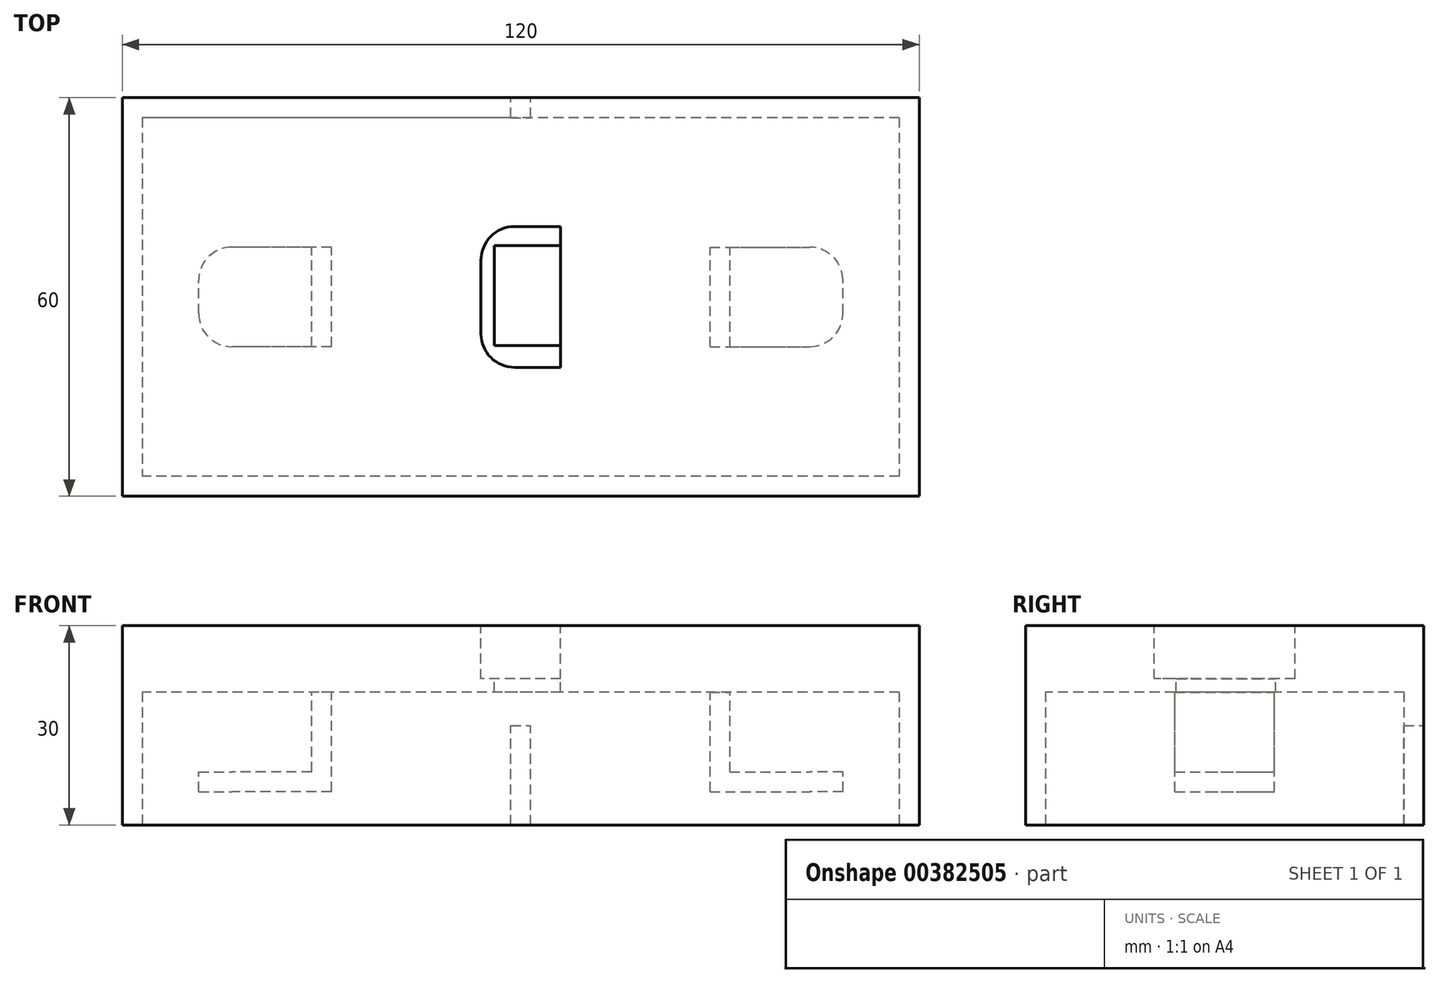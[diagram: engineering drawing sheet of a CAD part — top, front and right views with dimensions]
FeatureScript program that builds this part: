
annotation { "Feature Type Name" : "Feature", "Feature Type Description" : "" }
export const myFeature = defineFeature(function(context is Context, id is Id, definition is map)
    precondition{}
    {
        {
            var Q0;
            Q0=qCreatedBy(makeId("Top.planeOp"),FACE);
            var sketch = newSketch(context, id + "F0", { "sketchPlane" : qUnion([Q0])});
            skLineSegment(sketch, "E0.bottom", {"start": v(60, 30) * mm, "end": v(-60, 30) * mm});
            skLineSegment(sketch, "E0.top", {"start": v(60, -30) * mm, "end": v(-60, -30) * mm});
            skLineSegment(sketch, "E0.left", {"start": v(60, 30) * mm, "end": v(60, -30) * mm});
            skLineSegment(sketch, "E0.right", {"start": v(-60, 30) * mm, "end": v(-60, -30) * mm});
            skPoint(sketch, "E0.middle", {"position": v(0, 0) * mm});
            skSolve(sketch);
        }
        {
            var Q0;
            Q0 = qSketchRegion(id + "F0", true);
            extrude(context, id + "F1", {"entities" : qUnion([Q0]), "depth" : 30 * mm});
        }
        {
            var Q0;
            Q0=makeQuery(id+"F1.opExtrude","CAP_FACE",FACE,{"disambiguationData":[OSD([sQuery(id+"F0.wireOp",EDGE,"E0.bottom"),sQuery(id+"F0.wireOp",EDGE,"E0.top"),sQuery(id+"F0.wireOp",EDGE,"E0.left"),sQuery(id+"F0.wireOp",EDGE,"E0.right")])],"isStart":false});
            var sketch = newSketch(context, id + "F2", { "sketchPlane" : qUnion([Q0])});
            skLineSegment(sketch, "E1.bottom", {"start": v(6, 10.6) * mm, "end": v(-6, 10.6) * mm});
            skLineSegment(sketch, "E1.top", {"start": v(6, -10.6) * mm, "end": v(-6, -10.6) * mm});
            skLineSegment(sketch, "E1.left", {"start": v(6, 10.6) * mm, "end": v(6, -10.6) * mm});
            skLineSegment(sketch, "E1.right", {"start": v(-6, 10.6) * mm, "end": v(-6, -10.6) * mm});
            skPoint(sketch, "E1.middle", {"position": v(0, 0) * mm});
            skSolve(sketch);
        }
        {
            var Q0;
            Q0 = qSketchRegion(id + "F2", true);
            extrude(context, id + "F3", {"entities" : qUnion([Q0]), "operationType" : NewBodyOperationType.REMOVE, "oppositeDirection" : true, "depth" : 8 * mm});
        }
        {
            var Q0;
            Q0=makeQuery(id+"F1.opExtrude","CAP_FACE",FACE,{"disambiguationData":[OSD([sQuery(id+"F0.wireOp",EDGE,"E0.bottom"),sQuery(id+"F0.wireOp",EDGE,"E0.top"),sQuery(id+"F0.wireOp",EDGE,"E0.left"),sQuery(id+"F0.wireOp",EDGE,"E0.right")])],"isStart":true});
            var sketch = newSketch(context, id + "F4", { "sketchPlane" : qUnion([Q0])});
            skLineSegment(sketch, "E2.bottom", {"start": v(57, -27) * mm, "end": v(-57, -27) * mm});
            skLineSegment(sketch, "E2.top", {"start": v(57, 27) * mm, "end": v(-57, 27) * mm});
            skLineSegment(sketch, "E2.left", {"start": v(57, -27) * mm, "end": v(57, 27) * mm});
            skLineSegment(sketch, "E2.right", {"start": v(-57, -27) * mm, "end": v(-57, 27) * mm});
            skPoint(sketch, "E2.middle", {"position": v(0, 0) * mm});
            skSolve(sketch);
        }
        {
            var Q0;
            Q0 = qSketchRegion(id + "F4", true);
            extrude(context, id + "F5", {"entities" : qUnion([Q0]), "operationType" : NewBodyOperationType.REMOVE, "oppositeDirection" : true, "depth" : 20 * mm});
        }
        {
            var Q0;
            Q0=makeQuery(id+"F5.boolean.opBoolean","COPY",FACE,{"derivedFrom":makeQuery(id+"F5.opExtrude","CAP_FACE",FACE,{"disambiguationData":[OSD([sQuery(id+"F4.wireOp",EDGE,"E2.bottom"),sQuery(id+"F4.wireOp",EDGE,"E2.top"),sQuery(id+"F4.wireOp",EDGE,"E2.left"),sQuery(id+"F4.wireOp",EDGE,"E2.right")])],"isStart":false})});
            var sketch = newSketch(context, id + "F6", { "sketchPlane" : qUnion([Q0])});
            skLineSegment(sketch, "E3.bottom", {"start": v(-28.5, 7.5) * mm, "end": v(-31.5, 7.5) * mm});
            skLineSegment(sketch, "E3.top", {"start": v(-28.5, -7.5) * mm, "end": v(-31.5, -7.5) * mm});
            skLineSegment(sketch, "E3.left", {"start": v(-28.5, 7.5) * mm, "end": v(-28.5, -7.5) * mm});
            skLineSegment(sketch, "E3.right", {"start": v(-31.5, 7.5) * mm, "end": v(-31.5, -7.5) * mm});
            skPoint(sketch, "E3.middle", {"position": v(-30, 0) * mm});
            skPoint(sketch, "E4.MirrorP", {"position": v(30, 0) * mm});
            skLineSegment(sketch, "E5.MirrorCS", {"start": v(31.5, 7.5) * mm, "end": v(31.5, -7.5) * mm});
            skLineSegment(sketch, "E6.MirrorCS", {"start": v(28.5, 7.5) * mm, "end": v(28.5, -7.5) * mm});
            skLineSegment(sketch, "E7.MirrorCS", {"start": v(28.5, 7.5) * mm, "end": v(31.5, 7.5) * mm});
            skLineSegment(sketch, "E8.MirrorCS", {"start": v(28.5, -7.5) * mm, "end": v(31.5, -7.5) * mm});
            skSolve(sketch);
        }
        {
            var Q0;
            Q0 = qSketchRegion(id + "F6", true);
            extrude(context, id + "F7", {"entities" : qUnion([Q0]), "operationType" : NewBodyOperationType.ADD, "depth" : 12 * mm});
        }
        {
            var Q0;
            Q0=makeQuery(id+"F7.opExtrude","CAP_FACE",FACE,{"disambiguationData":[OSD([sQuery(id+"F6.wireOp",EDGE,"E3.bottom"),sQuery(id+"F6.wireOp",EDGE,"E3.top"),sQuery(id+"F6.wireOp",EDGE,"E3.left"),sQuery(id+"F6.wireOp",EDGE,"E3.right")])],"isStart":false});
            var sketch = newSketch(context, id + "F8", { "sketchPlane" : qUnion([Q0])});
            skLineSegment(sketch, "E9.bottom", {"start": v(-28.5, 7.5) * mm, "end": v(-48.5, 7.5) * mm});
            skLineSegment(sketch, "E9.top", {"start": v(-28.5, -7.5) * mm, "end": v(-48.5, -7.5) * mm});
            skLineSegment(sketch, "E9.left", {"start": v(-28.5, 7.5) * mm, "end": v(-28.5, -7.5) * mm});
            skLineSegment(sketch, "E9.right", {"start": v(-48.5, 7.5) * mm, "end": v(-48.5, -7.5) * mm});
            skLineSegment(sketch, "E10.MirrorCS", {"start": v(48.5, 7.5) * mm, "end": v(48.5, -7.5) * mm});
            skLineSegment(sketch, "E11.MirrorCS", {"start": v(28.5, 7.5) * mm, "end": v(28.5, -7.5) * mm});
            skLineSegment(sketch, "E12.MirrorCS", {"start": v(28.5, -7.5) * mm, "end": v(48.5, -7.5) * mm});
            skLineSegment(sketch, "E13.MirrorCS", {"start": v(28.5, 7.5) * mm, "end": v(48.5, 7.5) * mm});
            skSolve(sketch);
        }
        {
            var Q0;
            Q0 = qSketchRegion(id + "F8", true);
            extrude(context, id + "F9", {"entities" : qUnion([Q0]), "operationType" : NewBodyOperationType.ADD, "depth" : 3 * mm});
        }
        {
            var Q0;
            Q0=makeQuery(id+"F9.opExtrude","SWEPT_EDGE",EDGE,{"disambiguationData":[OSD([sQuery(id+"F8.wireOp",EDGE,"E9.bottom"),sQuery(id+"F8.wireOp",EDGE,"E9.right")])]});
            var Q1;
            Q1=makeQuery(id+"F9.opExtrude","SWEPT_EDGE",EDGE,{"disambiguationData":[OSD([sQuery(id+"F8.wireOp",EDGE,"E9.top"),sQuery(id+"F8.wireOp",EDGE,"E9.right")])]});
            var Q2;
            Q2=makeQuery(id+"F9.opExtrude","SWEPT_EDGE",EDGE,{"disambiguationData":[OSD([sQuery(id+"F8.wireOp",EDGE,"E10.MirrorCS"),sQuery(id+"F8.wireOp",EDGE,"E12.MirrorCS")])]});
            var Q3;
            Q3=makeQuery(id+"F9.opExtrude","SWEPT_EDGE",EDGE,{"disambiguationData":[OSD([sQuery(id+"F8.wireOp",EDGE,"E10.MirrorCS"),sQuery(id+"F8.wireOp",EDGE,"E13.MirrorCS")])]});
            fillet(context, id + "F10", {"entities" : qUnion([Q0, Q1, Q2, Q3]), "radius" : 5 * mm, "tangentPropagation" : true, "allowEdgeOverflow" : false});
        }
        {
            var Q0;
            Q0=makeQuery(id+"F3.boolean.opBoolean","COPY",EDGE,{"derivedFrom":makeQuery(id+"F3.opExtrude","SWEPT_EDGE",EDGE,{"disambiguationData":[OSD([sQuery(id+"F2.wireOp",EDGE,"E1.bottom"),sQuery(id+"F2.wireOp",EDGE,"E1.right")])]})});
            var Q1;
            Q1=makeQuery(id+"F3.boolean.opBoolean","COPY",EDGE,{"derivedFrom":makeQuery(id+"F3.opExtrude","SWEPT_EDGE",EDGE,{"disambiguationData":[OSD([sQuery(id+"F2.wireOp",EDGE,"E1.top"),sQuery(id+"F2.wireOp",EDGE,"E1.right")])]})});
            fillet(context, id + "F11", {"entities" : qUnion([Q0, Q1]), "radius" : 5.08 * mm, "tangentPropagation" : true, "allowEdgeOverflow" : false});
        }
        {
            var Q0;
            Q0=makeQuery(id+"F1.opExtrude","SWEPT_FACE",FACE,{"disambiguationData":[OSD([sQuery(id+"F0.wireOp",EDGE,"E0.bottom")])]});
            var sketch = newSketch(context, id + "F12", { "sketchPlane" : qUnion([Q0])});
            skLineSegment(sketch, "E14.bottom", {"start": v(1.5, 0) * mm, "end": v(-1.5, 0) * mm});
            skLineSegment(sketch, "E14.top", {"start": v(1.5, 15) * mm, "end": v(-1.5, 15) * mm});
            skLineSegment(sketch, "E14.left", {"start": v(1.5, 0) * mm, "end": v(1.5, 15) * mm});
            skLineSegment(sketch, "E14.right", {"start": v(-1.5, 0) * mm, "end": v(-1.5, 15) * mm});
            skPoint(sketch, "E14.middle", {"position": v(0, 7.5) * mm});
            skSolve(sketch);
        }
        {
            var Q0;
            Q0 = qSketchRegion(id + "F12", true);
            var Q1;
            Q1=makeQuery(id+"F5.boolean.opBoolean","COPY",FACE,{"derivedFrom":makeQuery(id+"F5.opExtrude","SWEPT_FACE",FACE,{"disambiguationData":[OSD([sQuery(id+"F4.wireOp",EDGE,"E2.bottom")])]})});
            extrude(context, id + "F13", {"entities" : qUnion([Q0]), "operationType" : NewBodyOperationType.REMOVE, "endBound" : BoundingType.UP_TO_NEXT, "oppositeDirection" : true, "endBoundEntityFace" : qUnion([Q1]), "depth" : 25 * mm});
        }
        {
            var Q0;
            Q0=makeQuery(id+"F3.boolean.opBoolean","COPY",FACE,{"derivedFrom":makeQuery(id+"F3.opExtrude","CAP_FACE",FACE,{"disambiguationData":[OSD([sQuery(id+"F2.wireOp",EDGE,"E1.bottom"),sQuery(id+"F2.wireOp",EDGE,"E1.top"),sQuery(id+"F2.wireOp",EDGE,"E1.left"),sQuery(id+"F2.wireOp",EDGE,"E1.right")])],"isStart":false})});
            var sketch = newSketch(context, id + "F14", { "sketchPlane" : qUnion([Q0])});
            skLineSegment(sketch, "E15.bottom", {"start": v(6, -7.29) * mm, "end": v(-4, -7.29) * mm});
            skLineSegment(sketch, "E15.top", {"start": v(6, 7.71) * mm, "end": v(-4, 7.71) * mm});
            skLineSegment(sketch, "E15.left", {"start": v(6, -7.29) * mm, "end": v(6, 7.71) * mm});
            skLineSegment(sketch, "E15.right", {"start": v(-4, -7.29) * mm, "end": v(-4, 7.71) * mm});
            skSolve(sketch);
        }
        {
            var Q0;
            Q0 = qSketchRegion(id + "F14", true);
            extrude(context, id + "F15", {"entities" : qUnion([Q0]), "operationType" : NewBodyOperationType.REMOVE, "endBound" : BoundingType.UP_TO_NEXT, "oppositeDirection" : true, "depth" : 25 * mm});
        }
    });
